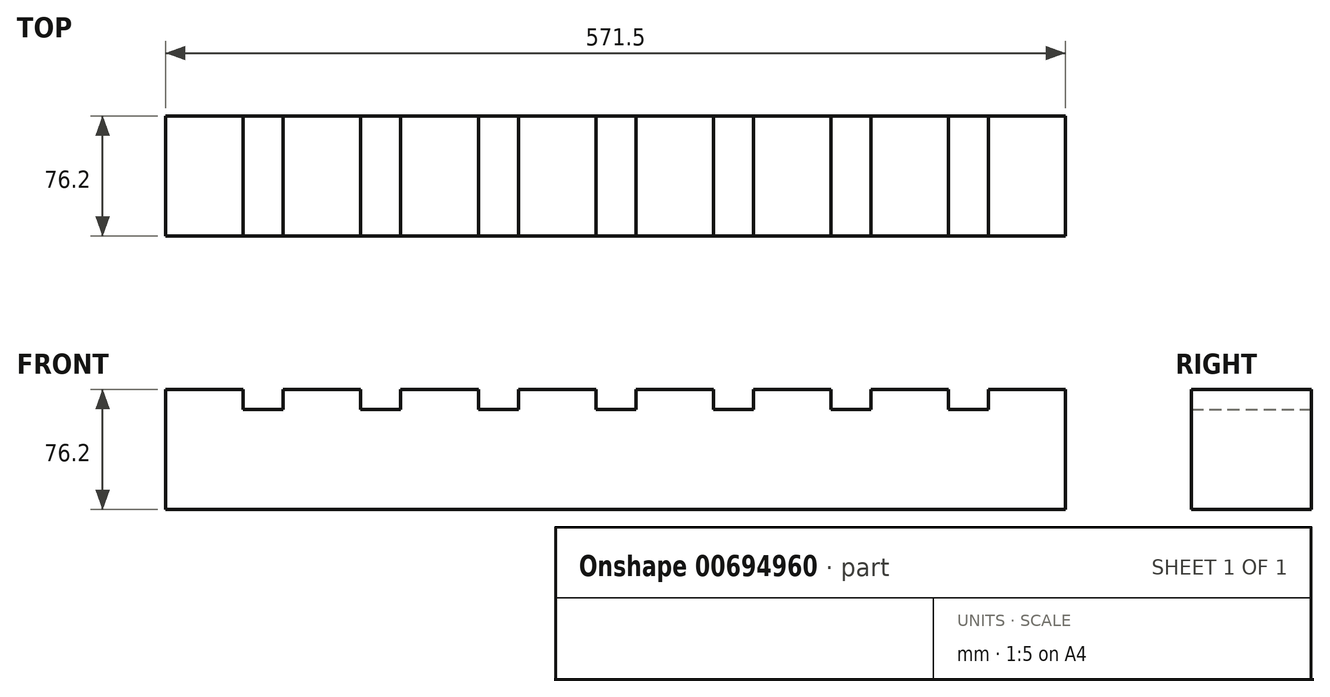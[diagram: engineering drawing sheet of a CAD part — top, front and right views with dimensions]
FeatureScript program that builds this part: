
annotation { "Feature Type Name" : "Feature", "Feature Type Description" : "" }
export const myFeature = defineFeature(function(context is Context, id is Id, definition is map)
    precondition{}
    {
        {
            var Q0;
            Q0=qCreatedBy(makeId("Front.planeOp"),FACE);
            var sketch = newSketch(context, id + "F0", { "sketchPlane" : qUnion([Q0])});
            skLineSegment(sketch, "E0.bottom", {"start": v(-285.75, 38.1) * mm, "end": v(-236.47, 38.1) * mm});
            skLineSegment(sketch, "E0.top", {"start": v(-285.75, -38.1) * mm, "end": v(285.75, -38.1) * mm});
            skLineSegment(sketch, "E0.left", {"start": v(-285.75, 38.1) * mm, "end": v(-285.75, -38.1) * mm});
            skLineSegment(sketch, "E0.right", {"start": v(285.75, 38.1) * mm, "end": v(285.75, -38.1) * mm});
            skPoint(sketch, "E0.middle", {"position": v(0, 0) * mm});
            skLineSegment(sketch, "E1.0", {"start": v(-285.75, 25.4) * mm, "end": v(285.75, 25.4) * mm, "construction": true});
            skLineSegment(sketch, "E2.bottom", {"start": v(-236.47, 25.4) * mm, "end": v(-211.07, 25.4) * mm});
            skLineSegment(sketch, "E2.left", {"start": v(-236.47, 25.4) * mm, "end": v(-236.47, 50.8) * mm});
            skLineSegment(sketch, "E2.right", {"start": v(-211.07, 25.4) * mm, "end": v(-211.07, 50.8) * mm});
            skLineSegment(sketch, "E3.1.0.0", {"start": v(-161.8, 25.4) * mm, "end": v(-136.4, 25.4) * mm});
            skLineSegment(sketch, "E3.1.0.2", {"start": v(-161.8, 25.4) * mm, "end": v(-161.8, 50.8) * mm});
            skLineSegment(sketch, "E3.1.0.3", {"start": v(-136.4, 25.4) * mm, "end": v(-136.4, 50.8) * mm});
            skLineSegment(sketch, "E3.2.0.0", {"start": v(-87.12, 25.4) * mm, "end": v(-61.72, 25.4) * mm});
            skLineSegment(sketch, "E3.2.0.2", {"start": v(-87.12, 25.4) * mm, "end": v(-87.12, 50.8) * mm});
            skLineSegment(sketch, "E3.2.0.3", {"start": v(-61.72, 25.4) * mm, "end": v(-61.72, 50.8) * mm});
            skLineSegment(sketch, "E3.3.0.0", {"start": v(-12.45, 25.4) * mm, "end": v(12.95, 25.4) * mm});
            skLineSegment(sketch, "E3.3.0.2", {"start": v(-12.45, 25.4) * mm, "end": v(-12.45, 50.8) * mm});
            skLineSegment(sketch, "E3.3.0.3", {"start": v(12.95, 25.4) * mm, "end": v(12.95, 50.8) * mm});
            skLineSegment(sketch, "E3.4.0.0", {"start": v(62.23, 25.4) * mm, "end": v(87.63, 25.4) * mm});
            skLineSegment(sketch, "E3.4.0.2", {"start": v(62.23, 25.4) * mm, "end": v(62.23, 50.8) * mm});
            skLineSegment(sketch, "E3.4.0.3", {"start": v(87.63, 25.4) * mm, "end": v(87.63, 50.8) * mm});
            skLineSegment(sketch, "E3.5.0.0", {"start": v(136.9, 25.4) * mm, "end": v(162.3, 25.4) * mm});
            skLineSegment(sketch, "E3.5.0.2", {"start": v(136.9, 25.4) * mm, "end": v(136.9, 50.8) * mm});
            skLineSegment(sketch, "E3.5.0.3", {"start": v(162.3, 25.4) * mm, "end": v(162.3, 50.8) * mm});
            skLineSegment(sketch, "E3.6.0.0", {"start": v(211.58, 25.4) * mm, "end": v(236.98, 25.4) * mm});
            skLineSegment(sketch, "E3.6.0.2", {"start": v(211.58, 25.4) * mm, "end": v(211.58, 50.8) * mm});
            skLineSegment(sketch, "E3.6.0.3", {"start": v(236.98, 25.4) * mm, "end": v(236.98, 50.8) * mm});
            skLineSegment(sketch, "E3.direction1", {"start": v(-236.47, 25.4) * mm, "end": v(-161.8, 25.4) * mm, "construction": true});
            skLineSegment(sketch, "E4.trimOffspring", {"start": v(-211.07, 38.1) * mm, "end": v(-161.8, 38.1) * mm});
            skLineSegment(sketch, "E5.trimOffspring", {"start": v(-136.4, 38.1) * mm, "end": v(-87.12, 38.1) * mm});
            skLineSegment(sketch, "E6.trimOffspring", {"start": v(-61.72, 38.1) * mm, "end": v(-12.45, 38.1) * mm});
            skLineSegment(sketch, "E7.trimOffspring", {"start": v(12.95, 38.1) * mm, "end": v(62.23, 38.1) * mm});
            skLineSegment(sketch, "E8.trimOffspring", {"start": v(87.63, 38.1) * mm, "end": v(136.9, 38.1) * mm});
            skLineSegment(sketch, "E9.trimOffspring", {"start": v(162.3, 38.1) * mm, "end": v(211.58, 38.1) * mm});
            skLineSegment(sketch, "E10.trimOffspring", {"start": v(236.98, 38.1) * mm, "end": v(285.75, 38.1) * mm});
            skSolve(sketch);
        }
        {
            var Q0;
            Q0 = qSketchRegion(id + "F0", true);
            extrude(context, id + "F1", {"entities" : qUnion([Q0]), "endBound" : BoundingType.SYMMETRIC, "depth" : 76.2 * mm, "offsetDistance" : 25.4 * mm});
        }
    });
